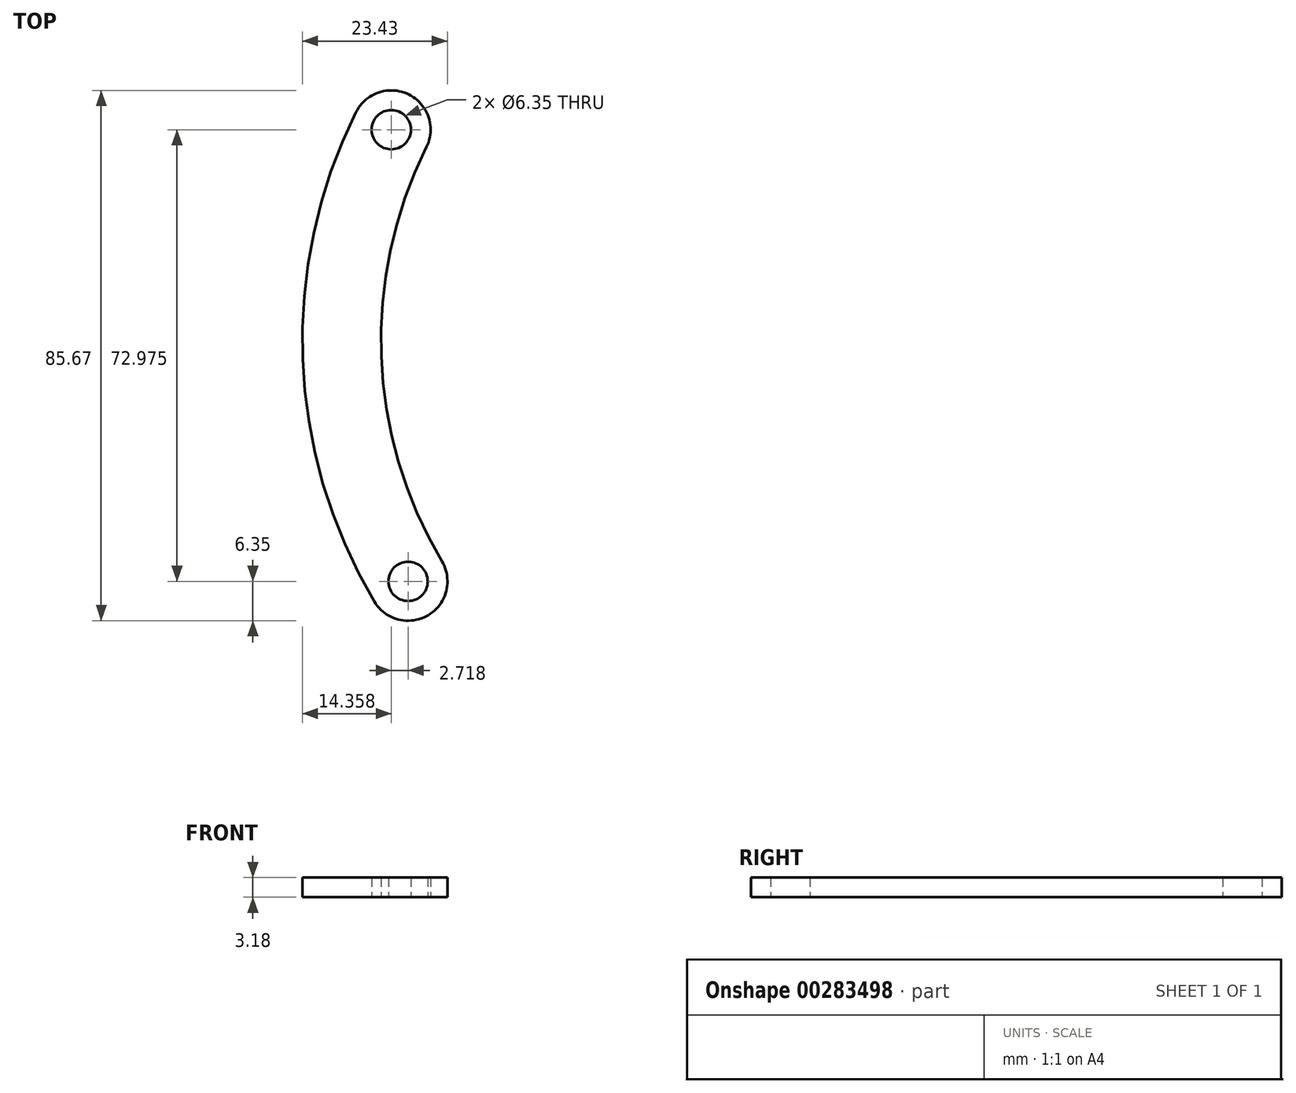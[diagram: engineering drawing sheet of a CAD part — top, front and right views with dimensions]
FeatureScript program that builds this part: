
annotation { "Feature Type Name" : "Feature", "Feature Type Description" : "" }
export const myFeature = defineFeature(function(context is Context, id is Id, definition is map)
    precondition{}
    {
        {
            var Q0;
            Q0=qCreatedBy(makeId("Top.planeOp"),FACE);
            var sketch = newSketch(context, id + "F0", { "sketchPlane" : qUnion([Q0])});
            skCircle(sketch, "E0", {"center": v(0, 0) * mm, "radius": 41.28 * mm, "construction": true});
            skCircle(sketch, "E1.0", {"center": v(0, 0) * mm, "radius": 34.93 * mm, "construction": true});
            skLineSegment(sketch, "E2", {"start": v(-7.63, -34.08) * mm, "end": v(0, 0) * mm, "construction": true});
            skLineSegment(sketch, "E3", {"start": v(0, 0) * mm, "end": v(30.94, -16.2) * mm, "construction": true});
            skLineSegment(sketch, "E4", {"start": v(40.64, 50.8) * mm, "end": v(-86.34, 52.78) * mm});
            skLineSegment(sketch, "E5", {"start": v(30.94, -16.2) * mm, "end": v(39.13, -133.7) * mm});
            skCircle(sketch, "E6", {"center": v(40.64, 50.8) * mm, "radius": 101.6 * mm, "construction": true});
            skLineSegment(sketch, "E7", {"start": v(-60.95, 52.39) * mm, "end": v(-60.95, 52.39) * mm});
            skLineSegment(sketch, "E8", {"start": v(-10.35, 38.9) * mm, "end": v(-7.63, -34.08) * mm, "construction": true});
            skCircle(sketch, "E9.0", {"center": v(0, 0) * mm, "radius": 28.57 * mm, "construction": true});
            skCircle(sketch, "E10.0", {"center": v(40.64, 50.8) * mm, "radius": 100.93 * mm});
            skLineSegment(sketch, "E11.0", {"start": v(5.89, 11.25) * mm, "end": v(36.83, -4.94) * mm});
            skLineSegment(sketch, "E12.0", {"start": v(-20.03, -31.3) * mm, "end": v(-12.4, 2.78) * mm});
            skLineSegment(sketch, "E13", {"start": v(-7.63, -34.08) * mm, "end": v(30.94, -16.2) * mm, "construction": true});
            skLineSegment(sketch, "E14.0", {"start": v(-2.3, -45.6) * mm, "end": v(36.28, -27.72) * mm});
            skArc(sketch, "E15.filletArc", {"start": v(-20.03, -31.3) * mm, "mid": v(-15.6, -43.97) * mm, "end": v(-2.3, -45.6) * mm});
            skArc(sketch, "E16.filletArc", {"start": v(36.28, -27.72) * mm, "mid": v(43.64, -16.5) * mm, "end": v(36.83, -4.94) * mm});
            skArc(sketch, "E17.filletArc", {"start": v(5.89, 11.25) * mm, "mid": v(-5.34, 11.52) * mm, "end": v(-12.4, 2.78) * mm});
            skCircle(sketch, "E18", {"center": v(0, 0) * mm, "radius": 6.35 * mm});
            skCircle(sketch, "E19", {"center": v(-7.63, -34.08) * mm, "radius": 3.18 * mm});
            skCircle(sketch, "E20", {"center": v(30.94, -16.2) * mm, "radius": 6.35 * mm});
            skLineSegment(sketch, "E21", {"start": v(-10.15, 51.6) * mm, "end": v(-10.35, 38.9) * mm});
            skCircle(sketch, "E22", {"center": v(-10.35, 38.9) * mm, "radius": 3.18 * mm});
            skArc(sketch, "E23", {"start": v(-10.35, 38.9) * mm, "mid": v(-18.3, 2.06) * mm, "end": v(-7.63, -34.08) * mm, "construction": true});
            skArc(sketch, "E24.0", {"start": v(-4.67, 36.06) * mm, "mid": v(-7.52, 44.58) * mm, "end": v(-16.03, 41.73) * mm});
            skArc(sketch, "E25.0", {"start": v(-16.03, 41.73) * mm, "mid": v(-24.65, 1.82) * mm, "end": v(-13.1, -37.33) * mm});
            skArc(sketch, "E26.0", {"start": v(-4.67, 36.06) * mm, "mid": v(-11.96, 2.3) * mm, "end": v(-2.18, -30.83) * mm});
            skArc(sketch, "E27.0", {"start": v(-13.1, -37.33) * mm, "mid": v(-4.39, -39.54) * mm, "end": v(-2.18, -30.83) * mm});
            skSolve(sketch);
        }
        {
            var Q0;
            Q0=makeQuery(id+"F0.imprint","IMPRINT",FACE,{"disambiguationData":[TD([[makeQuery(id+"F0.imprint","IMPRINT",EDGE,{"derivedFrom":sQuery(id+"F0.wireOp",EDGE,"E22")}),-1.0]])]});
            var Q1;
            Q1=makeQuery(id+"F0.imprint","IMPRINT",FACE,{"disambiguationData":[TD([[makeQuery(id+"F0.imprint","IMPRINT",EDGE,{"derivedFrom":sQuery(id+"F0.wireOp",EDGE,"E19")}),-1.0]])]});
            var Q2;
            {var subQ0=sQuery(id+"F0.wireOp",EDGE,"E25.0");var subQ1=sQuery(id+"F0.wireOp",EDGE,"E10.0");var subQ2=makeQuery(id+"F0.imprint","INTERSECT",VERTEX,{"derivedFrom":[subQ1,subQ0]});Q2=makeQuery(id+"F0.imprint","IMPRINT",FACE,{"disambiguationData":[TD([[makeQuery(id+"F0.imprint","IMPRINT",EDGE,{"disambiguationData":[TD([[subQ2,-1.0]])],"derivedFrom":subQ1}),-1.0]])]});}
            extrude(context, id + "F1", {"entities" : qUnion([Q0, Q1, Q2]), "depth" : 3.17 * mm});
        }
    });
